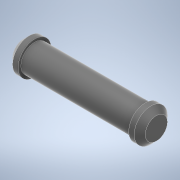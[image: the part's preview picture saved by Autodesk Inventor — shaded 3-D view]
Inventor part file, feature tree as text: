
AUTODESK INVENTOR PART (.ipt)
format: ipt  version: 2021 (Build 250183000, 183)  size: 117,760 bytes
history: native  units: mm
features: extrude x3, sketch x3, chamfer x2
ambient origin geometry x8: Origin, YZ Plane, XZ Plane, XY Plane, X Axis, Y Axis, Z Axis, Center Point
bodies: Solid1 (feature_tree)
feature tree (8):
  extrude  "Extrusion1"  Depth=20.0mm TaperAngle=0.0deg
  extrude  "Extrusion2"  Depth=2.0mm TaperAngle=0.0deg
  chamfer  "Chamfer1"  Distance=2.0mm Angle=45.0deg
  extrude  "Extrusion3"  Depth=2.0mm TaperAngle=45.0deg
  chamfer  "Chamfer2"  [1 undecoded]
  sketch  "Sketch1"  dims[d0=5.0mm d1=20.0mm d2=0.0mm]
  sketch  "Sketch2"  dims[d3=6.0mm d4=2.0mm d5=0.0mm d6=1.0mm d7=2.0mm d8=45.0deg]
  sketch  "Sketch3"  dims[d9=2.0mm d10=0.0mm d11=1.0mm d12=2.0mm d13=45.0deg]
note: 1 required parameter value undecoded (feature->parameter linkage not recoverable at this tier; creation-order binding heuristic only, values carry confidence <= 0.55)
